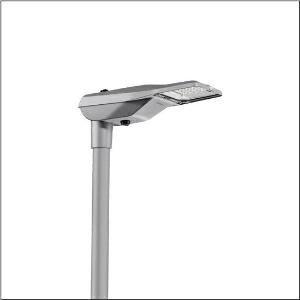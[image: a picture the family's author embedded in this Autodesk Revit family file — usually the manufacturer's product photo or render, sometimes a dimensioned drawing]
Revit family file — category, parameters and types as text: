
# Revit family: streetlight_sl_21_iq_micro___st1_0ab_5xe1m31y08cb_a08b
name_source: partatom
category: Lighting Fixtures
units: mm (PartAtom-declared; Revit-internal decimal feet)

## family parameters
Cut with Voids When Loaded = No
Host = Face
Light Source = No
Part Type = Normal
Room Calculation Point = No
Round Connector Dimension = Use Diameter
Shared = No

## types (1)
- --- (1 x LED, 2530 lm, 19.1 W, 3000K)
    Apparent Load = 19 VA
    CIE Flux Codes = 38 73 97 100 100
    Color Rendering = 70
    Color Temperature = 3000K
    Default Elevation = 1800 mm
    Description = Streetlight SL 21 iQ micro, mast luminaire, primary light control with lens, of PMMA, primary optical cover: cover, of toughened safety glass, transparent, light distribution: ST1.0aB, light emission: direct distribution, primary light characteristic: asymmetric, installation type: post-top, side-entry, LED, High Power LED, rated luminous flux: 2.530lm, luminous efficacy: 133lm/W, light colour: 730, colour temperature: 3000K, control: presetting dimming logarithmic, Street-Remote, Auto-Match, Temp-Guard, Lumen-Switch, Night-Set, Smart-Wire, Light-Fading, Desk-Remote (wireless, voltage-free reading and setting of iQ features in the workshop via application-optimized NFC function/RFID function), optimised constant luminous flux control (CLO 2.0), mains connection: 220..240V, AC, 50/60Hz, start of lifetime: 19W, end of service life: 20W, reduction: 9W, luminaire housing, of diecast aluminium, powder-coated, Siteco® metallic grey (DB 702S), corrosivity category C5 mid according to DIN EN ISO 12944, please order mast flange separately, inclination adjustable: 0°, 5°, 10°, 15°, sealing non-destructively replaceable, multi-level sealing system, length: 528mm, width: 235mm, height: 110mm, mast flange for spigot size: 42mm (side-entry): 5XC10008XM4, 60/48mm (side-entry/post-top): 5XC10108XM2, 76/60mm (side-entry/post-top): 5XC10108XM1, Smart Interface below and above, protection rating (complete): IP66, insulation class (complete): insulation class II (safety insulation), certification: CE, ENEC, ENEC+, VDE, impact resistance: IK09, permissible operating ambient temperature for outdoor applications: -40..+50°C, standard-compliant lighting for roads and squares, packaging unit: 1 piece

Light Distribution: ST1.0aB
    Height = 110 mm
    Lamp = 1 x LED
    Lamp Light Flux = 2530 lm
    Lamp Power = 19.1 W
    Lamp count = 1
    Length = 528 mm
    Luminous efficacy = 132 lm/W
    Manufacturer = Siteco
    ModVariant = No
    Model = 5XE1M31Y08CB
    Number of Poles = 1
    OnlyDefault = Yes
    Power Factor = 1
    Product Name = Streetlight SL 21 iQ micro | ST1.0aB
    Product group = mast luminaire | pylon top
    ProductGroupID = 6100
    Protection Class = Protection class II
    Protection Degree = IP 66
    RLX_Detail_Level = 1
    RLX_Emergency_Light_Flux = 0 lm
    RLX_Emergency_Type = 0
    RLX_Emergency_Type_DB = No
    RlxData = <blob elided: 98565 chars, md5=de747870>
    Socket = socket
    Standby Power = 0 W
    System Light Flux = 2530 lm
    System Power = 19 W
    Type Comments = factory setting: luminous flux: 100 % | dim-lin: 254 | 387 mA
    Type Image = l_1007239.jpg
    URL = http://relux.com
    VarID = @adj_060913
    Voltage = 0 V
    Weight = 0.00 kg
    Width = 235 mm

## geometry (parser evidence)
native form markers: Blend x4, Sweep x10
no freeform markers — native parametric forms only
